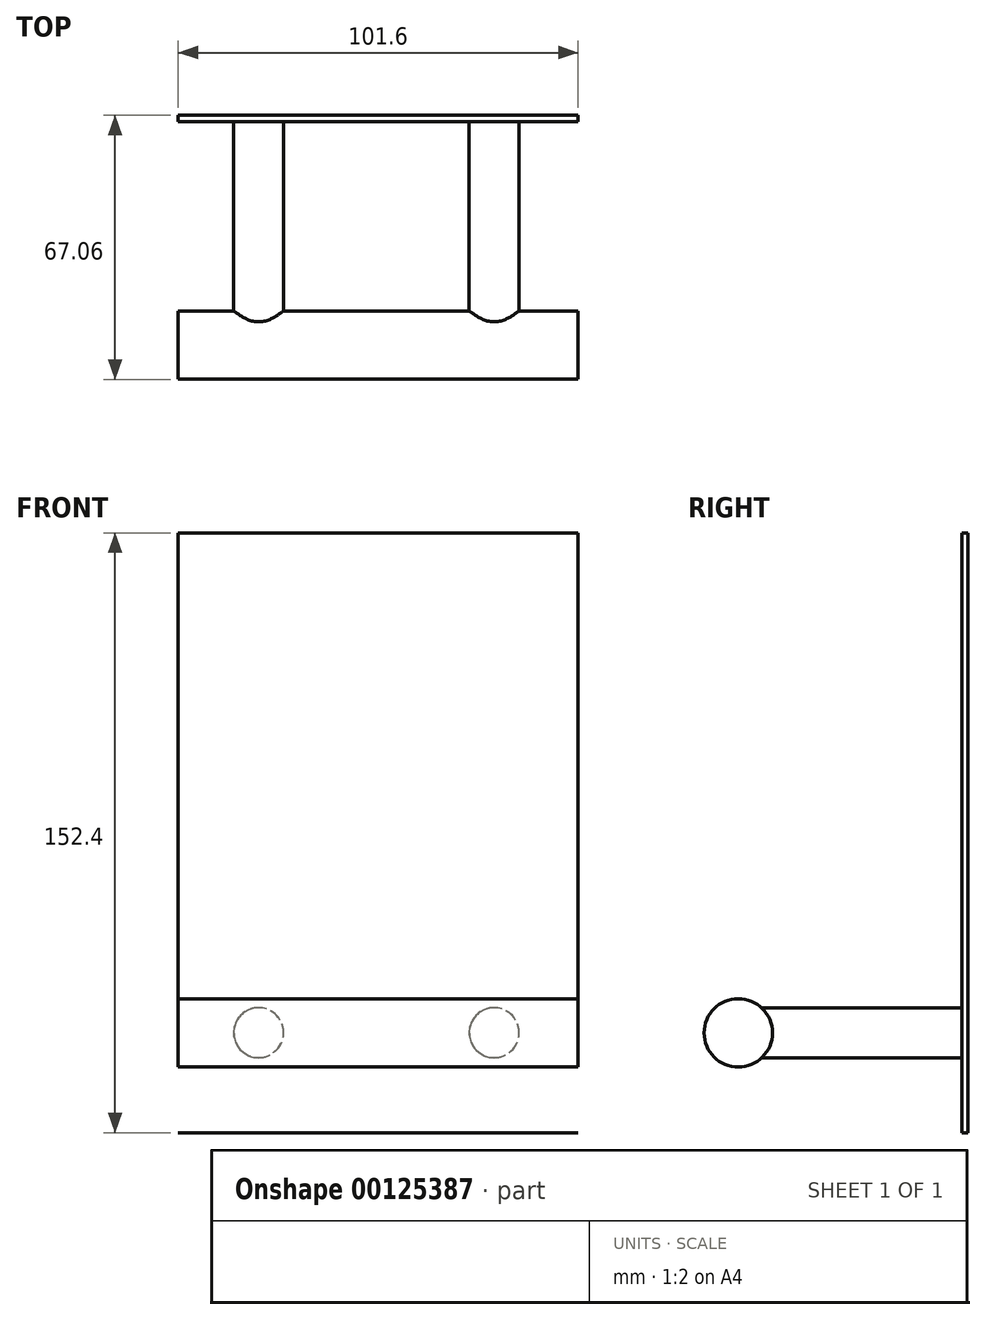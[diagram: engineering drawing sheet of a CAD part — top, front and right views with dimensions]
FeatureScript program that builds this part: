
annotation { "Feature Type Name" : "Feature", "Feature Type Description" : "" }
export const myFeature = defineFeature(function(context is Context, id is Id, definition is map)
    precondition{}
    {
        {
            var Q0;
            Q0=qCreatedBy(makeId("Front.planeOp"),FACE);
            var sketch = newSketch(context, id + "F0", { "sketchPlane" : qUnion([Q0])});
            skLineSegment(sketch, "E0", {"start": v(-50.8, 76.2) * mm, "end": v(-50.8, 0) * mm});
            skLineSegment(sketch, "E1", {"start": v(-50.8, 76.2) * mm, "end": v(0, 76.2) * mm});
            skLineSegment(sketch, "E2.MirrorCS", {"start": v(50.8, 76.2) * mm, "end": v(50.8, 0) * mm});
            skLineSegment(sketch, "E3.MirrorCS", {"start": v(50.8, 76.2) * mm, "end": v(0, 76.2) * mm});
            skLineSegment(sketch, "E4.MirrorCS", {"start": v(-50.8, -76.2) * mm, "end": v(-50.8, 0) * mm});
            skLineSegment(sketch, "E5.MirrorCS", {"start": v(-50.8, -76.2) * mm, "end": v(0, -76.2) * mm});
            skLineSegment(sketch, "E6.MirrorCS", {"start": v(50.8, -76.2) * mm, "end": v(0, -76.2) * mm});
            skLineSegment(sketch, "E7.MirrorCS", {"start": v(50.8, -76.2) * mm, "end": v(50.8, 0) * mm});
            skSolve(sketch);
        }
        {
            var Q0;
            Q0 = qSketchRegion(id + "F0", true);
            extrude(context, id + "F1", {"entities" : qUnion([Q0]), "depth" : 1.6 * mm});
        }
        {
            var Q0;
            Q0=makeQuery(id+"F1.opExtrude","CAP_FACE",FACE,{"disambiguationData":[OSD([sQuery(id+"F0.wireOp",EDGE,"E0"),sQuery(id+"F0.wireOp",EDGE,"E1"),sQuery(id+"F0.wireOp",EDGE,"E2.MirrorCS"),sQuery(id+"F0.wireOp",EDGE,"E3.MirrorCS"),sQuery(id+"F0.wireOp",EDGE,"E4.MirrorCS"),sQuery(id+"F0.wireOp",EDGE,"E5.MirrorCS"),sQuery(id+"F0.wireOp",EDGE,"E6.MirrorCS"),sQuery(id+"F0.wireOp",EDGE,"E7.MirrorCS")])],"isStart":false});
            var sketch = newSketch(context, id + "F2", { "sketchPlane" : qUnion([Q0])});
            skCircle(sketch, "E8", {"center": v(-30.37, -50.8) * mm, "radius": 6.35 * mm});
            skCircle(sketch, "E9", {"center": v(29.48, -50.8) * mm, "radius": 6.35 * mm});
            skSolve(sketch);
        }
        {
            var Q0;
            Q0 = qSketchRegion(id + "F2", true);
            extrude(context, id + "F3", {"entities" : qUnion([Q0]), "operationType" : NewBodyOperationType.ADD, "depth" : 50.8 * mm});
        }
        {
            var Q0;
            Q0=qCreatedBy(makeId("Right.planeOp"),FACE);
            var sketch = newSketch(context, id + "F4", { "sketchPlane" : qUnion([Q0])});
            skCircle(sketch, "E10", {"center": v(-58.37, -50.84) * mm, "radius": 8.69 * mm});
            skSolve(sketch);
        }
        {
            var Q0;
            Q0 = qSketchRegion(id + "F4", true);
            extrude(context, id + "F5", {"entities" : qUnion([Q0]), "operationType" : NewBodyOperationType.ADD, "depth" : 50.8 * mm, "hasSecondDirection" : true, "secondDirectionOppositeDirection" : true, "secondDirectionDepth" : 50.8 * mm});
        }
    });
